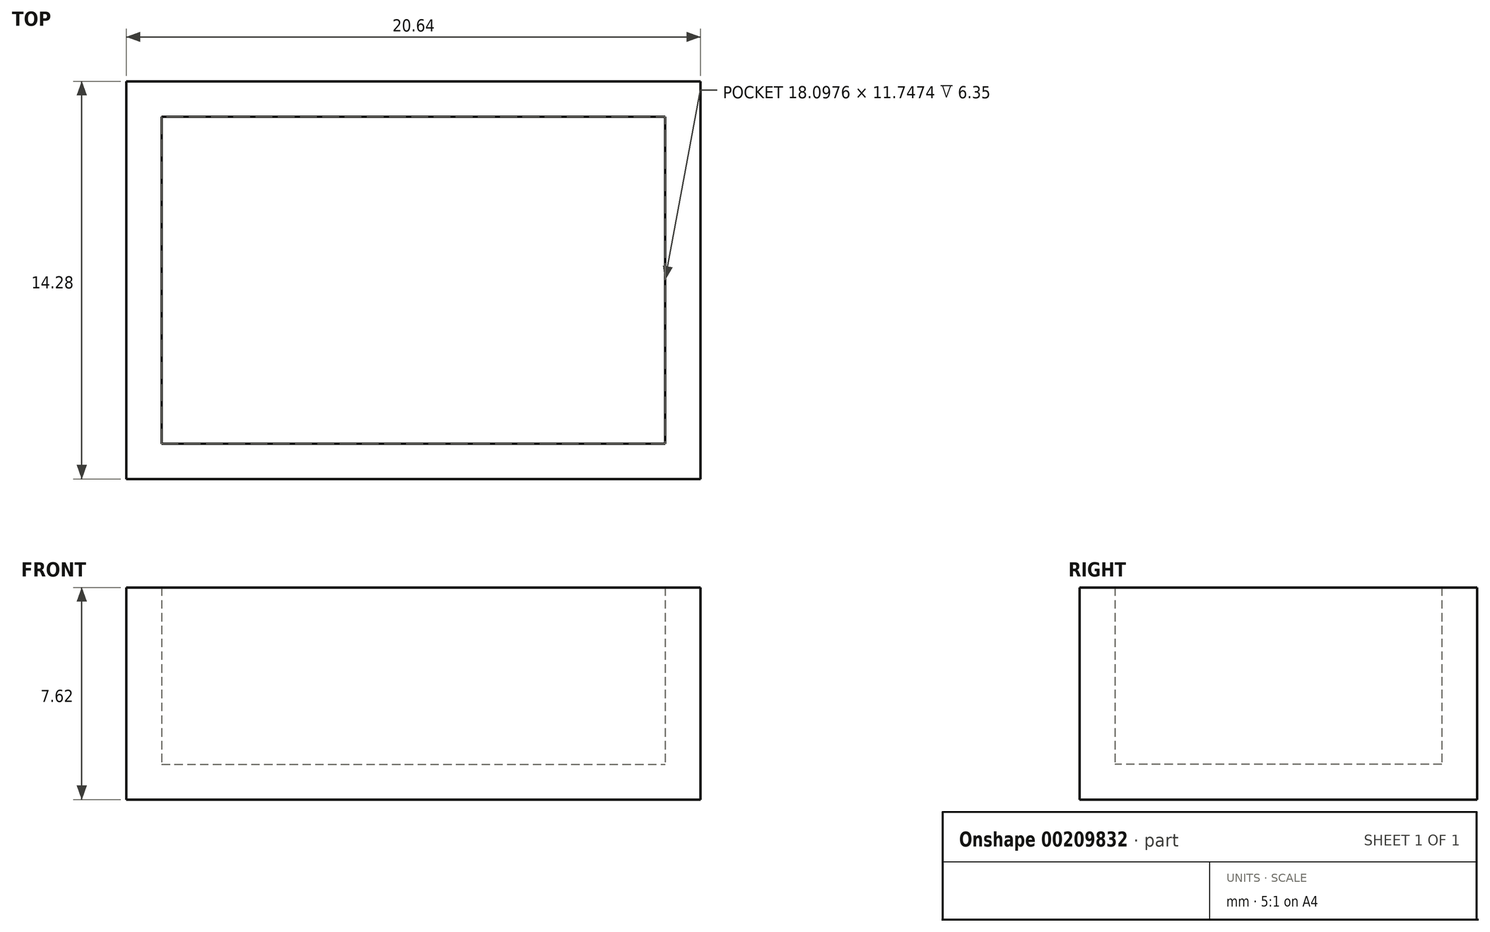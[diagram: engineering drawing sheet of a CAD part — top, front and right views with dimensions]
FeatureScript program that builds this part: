
annotation { "Feature Type Name" : "Feature", "Feature Type Description" : "" }
export const myFeature = defineFeature(function(context is Context, id is Id, definition is map)
    precondition{}
    {
        {
            var Q0;
            Q0=qCreatedBy(makeId("Top.planeOp"),FACE);
            var sketch = newSketch(context, id + "F0", { "sketchPlane" : qUnion([Q0])});
            skLineSegment(sketch, "E0.bottom", {"start": v(10.32, 7.14) * mm, "end": v(-10.32, 7.14) * mm});
            skLineSegment(sketch, "E0.top", {"start": v(10.32, -7.14) * mm, "end": v(-10.32, -7.14) * mm});
            skLineSegment(sketch, "E0.left", {"start": v(10.32, 7.14) * mm, "end": v(10.32, -7.14) * mm});
            skLineSegment(sketch, "E0.right", {"start": v(-10.32, 7.14) * mm, "end": v(-10.32, -7.14) * mm});
            skPoint(sketch, "E0.middle", {"position": v(0, 0) * mm});
            skSolve(sketch);
        }
        {
            var Q0;
            Q0=makeQuery(id+"F0.imprint","IMPRINT",FACE,{"disambiguationData":[TD([[makeQuery(id+"F0.imprint","IMPRINT",EDGE,{"derivedFrom":sQuery(id+"F0.wireOp",EDGE,"E0.bottom")}),1.0]])]});
            extrude(context, id + "F1", {"entities" : qUnion([Q0]), "depth" : 1.27 * mm});
        }
        {
            var Q0;
            Q0=makeQuery(id+"F1.opExtrude","CAP_FACE",FACE,{"disambiguationData":[OSD([sQuery(id+"F0.wireOp",EDGE,"E0.bottom"),sQuery(id+"F0.wireOp",EDGE,"E0.top"),sQuery(id+"F0.wireOp",EDGE,"E0.left"),sQuery(id+"F0.wireOp",EDGE,"E0.right")])],"isStart":false});
            var sketch = newSketch(context, id + "F2", { "sketchPlane" : qUnion([Q0])});
            skLineSegment(sketch, "E1.bottom", {"start": v(-10.32, 7.14) * mm, "end": v(10.32, 7.14) * mm});
            skLineSegment(sketch, "E1.top", {"start": v(-10.32, -7.14) * mm, "end": v(10.32, -7.14) * mm});
            skLineSegment(sketch, "E1.left", {"start": v(-10.32, 7.14) * mm, "end": v(-10.32, -7.14) * mm});
            skLineSegment(sketch, "E1.right", {"start": v(10.32, 7.14) * mm, "end": v(10.32, -7.14) * mm});
            skPoint(sketch, "E1.middle", {"position": v(0, 0) * mm});
            skLineSegment(sketch, "E2.bottom", {"start": v(-9.05, 5.87) * mm, "end": v(9.05, 5.87) * mm});
            skLineSegment(sketch, "E2.top", {"start": v(-9.05, -5.87) * mm, "end": v(9.05, -5.87) * mm});
            skLineSegment(sketch, "E2.left", {"start": v(-9.05, 5.87) * mm, "end": v(-9.05, -5.87) * mm});
            skLineSegment(sketch, "E2.right", {"start": v(9.05, 5.87) * mm, "end": v(9.05, -5.87) * mm});
            skSolve(sketch);
        }
        {
            var Q0;
            Q0=makeQuery(id+"F2.imprint","IMPRINT",FACE,{"disambiguationData":[TD([[makeQuery(id+"F2.imprint","IMPRINT",EDGE,{"derivedFrom":sQuery(id+"F2.wireOp",EDGE,"E1.bottom")}),1.0]])]});
            extrude(context, id + "F3", {"entities" : qUnion([Q0]), "operationType" : NewBodyOperationType.ADD, "depth" : 6.35 * mm});
        }
    });
